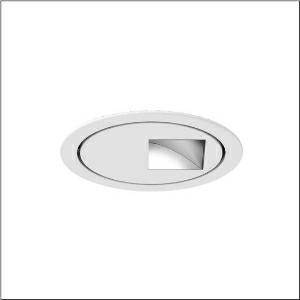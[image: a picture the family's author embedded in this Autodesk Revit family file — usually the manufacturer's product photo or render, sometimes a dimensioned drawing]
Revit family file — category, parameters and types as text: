
# Revit family: lunis_11_mini_round_51dk11b72wn21
name_source: partatom
category: Lighting Fixtures
units: mm (PartAtom-declared; Revit-internal decimal feet)

## family parameters
Cut with Voids When Loaded = No
Host = Face
Light Source = No
Part Type = Normal
Room Calculation Point = No
Round Connector Dimension = Use Diameter
Shared = No

## types (1)
- Lunis 11 mini round (1 x LED 4000K / CRI = 90 (unbekannt), 2120 lm, 4000K)
    Apparent Load = 28 VA
    CIE Flux Codes = 44 77 97 100 100
    Color Rendering = 90
    Color Temperature = 4000K
    Default Elevation = 1800 mm
    Description = Lunis 11 mini round, downlight, light control with wallwasher, of highly reflective aluminium, highly specular, light emission: direct distribution, LED rated luminous flux: 2.120lm, light colour: 940, control gear: ECG, with terminal, 3-pole, mains connection: 220..230V, AC/DC, 0/50..60Hz, LED module, luminaire module, of aluminium, highly specular, white, diameter: 176mm, clamping range: 1..40mm, recessing ring, of plastic, traffic white (RAL 9016), protection rating (complete): IP20, insulation class (complete): insulation class II (safety insulation), certification: CE, permissible ambient temperature for indoor applications: 0..+35°C, packaging unit: 1 piece
    Height = 0 mm  [stored 0 ft]
    Lamp = 1 x LED 4000K / CRI >= 90 (unbekannt)
    Lamp Light Flux = 2120 lm
    Lamp count = 1
    Length = 176 mm
    Luminous efficacy = 75 lm/W
    Manufacturer = Siteco
    ModVariant = No
    Model = 51DK11B72WN21
    Mounting Place = Ceiling
    Mounting Type = Recessed
    Number of Poles = 1
    OnlyDefault = Yes
    Power Factor = 1
    Product Name = Lunis 11 mini round
    Product group = downlight
    ProductGroupID = 401
    Protection Class = Protection class II
    Protection Degree = IP 20
    RLX_Detail_Level = 1
    RLX_Emergency_Light_Flux = 0 lm
    RLX_Emergency_Type = 0
    RLX_Emergency_Type_DB = No
    RlxData = <blob elided: 59345 chars, md5=9b1ed624>
    Socket = socket
    Standby Power = 0 W
    System Light Flux = 2120 lm
    System Power = 28 W
    Type Comments = Product without accessories
    Type Image = l_1004772.jpg
    URL = http://relux.com
    VarID = ---
    Voltage = 0 V
    Weight = 0.00 kg
    Width = 176 mm

note: [stored X ft] marks values corroborated as IEEE doubles in the binary element streams (Revit-internal decimal feet)

## geometry (parser evidence)
native form markers: Blend x4, Sweep x11
no freeform markers — native parametric forms only
